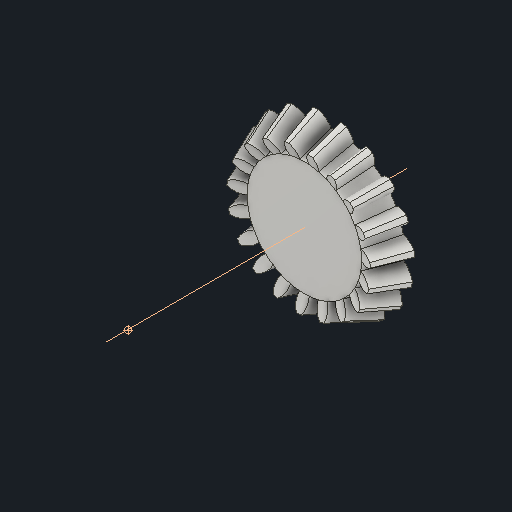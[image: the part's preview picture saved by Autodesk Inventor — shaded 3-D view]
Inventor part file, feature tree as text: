
AUTODESK INVENTOR PART (.ipt)
format: ipt  version: 2022 (Build 260153000, 153)  size: 572,416 bytes
history: native  units: mm
features: other x24, loft x2, pattern_circular x2, sketch x1
ambient origin geometry x6: Origin, XZ Plane, X Axis, Y Axis, Z Axis, Center Point
bodies: Solid1 (feature_tree)
feature tree (29):
  other  "Top Point"
  other  "Mesh Plane2"
  other  "Teeth Body"
  other  "Start Point"
  other  "Tooth Plane"
  other  "Start Sketch"
  other  "End Point"
  other  "3D Sketch Right"
  other  "End Plane Right"
  loft  "Loft Right"
  pattern_circular  "Circular Pattern Right"  [2 undecoded]
  other  "3D Sketch Left"
  other  "End Plane Left"
  loft  "Loft Left"
  pattern_circular  "Circular Pattern Left"  [2 undecoded]
  other  "Fix Body"
  other  "Mesh Plane"
  other  "Top Plane"
  other  "Teeth Body Sketch"
  other  "End Plane"
  other  "End Sketch"
  other  "Helical Curve Left"
  other  "End Sketch Left"
  other  "Body Sketch"
  sketch  "Sketch6"  dims[d0=47.5mm d1=40.16154mm d2=50.389413mm d3=10.0mm d4=59.428137mm d5=90.0deg d7=6.612538mm d8=8.167518mm d9=22.385367mm d11=10.275mm d12=5.559628mm d15=6.867009mm d16=18.820959mm d17=0.0mm d18=90.0deg d19=0.0mm d20=90.0deg d21=190.0mm d22=360.0deg d26=351.677194mm d27=9.553763mm d28=47.5mm d29=-3.769093mm d30=5.559628mm d31=6.867009mm d32=18.820959mm d35=0.0mm d37=0.0mm d39=0.0mm d40=90.0deg d41=190.0mm d42=360.0deg d46=90.0deg d47=90.0deg d48=0.0mm d49=0.0mm d50=90.0deg d51=1.65347mm d52=0.0mm d53=0.0mm d54=0.0mm d56=19.795916mm d57=28.746717mm d58=20.936717mm d59=24.169395mm d60=17.602976mm d61=24.169395mm d62=17.602976mm d65=351.677194mm d66=31.5mm d67=47.5mm d68=-3.769093mm d69=9.553763mm d70=6.867009mm d71=18.820959mm d72=5.559628mm d73=17.602976mm d74=24.169395mm d75=0.0mm d77=0.0mm d79=0.0mm d80=90.0deg d81=190.0mm d82=360.0deg d84=10.0mm d85=20.0mm d86=20.0mm d87=10.0mm d88=0.0mm d89=0.0mm d90=90.0deg d91=90.0deg d92=90.0deg d93=90.0deg]
  other  "Srf1"
  other  "Helical Curve Right"
  other  "End Sketch Right"
  other  "Pitch Diameter"
note: 4 required parameter values undecoded (feature->parameter linkage not recoverable at this tier; creation-order binding heuristic only, values carry confidence <= 0.55)
